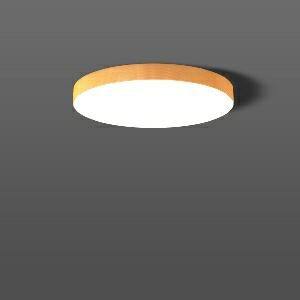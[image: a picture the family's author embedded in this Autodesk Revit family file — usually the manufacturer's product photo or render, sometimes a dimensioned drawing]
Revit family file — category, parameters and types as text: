
# Revit family: flatliner_slim_312281_002_1_76_adea
name_source: partatom
category: Lighting Fixtures
units: mm (PartAtom-declared; Revit-internal decimal feet)

## family parameters
Cut with Voids When Loaded = No
Host = Face
Light Source = No
Part Type = Normal
Room Calculation Point = No
Round Connector Dimension = Use Diameter
Shared = No

## types (1)
- 982556.002 (1 x LED Modul 840, 1700 lm, 4000)
    Apparent Load = 21 VA
    CIE Flux Codes = 45 76 94 95 100
    Color Rendering = 80
    Color Temperature = 4000
    Default Elevation = 1800 mm
    Description = Series: FLATLINER SLIM
Decorative ceiling luminaire for interior decoration. Base luminaire prepared for the installation of fabric lampshade. Base: metal, white, powder-coated. TouchDim sensor capable. Light and/or presence sensors can be integrated. Modular design: with the basic luminaire, a cylindrical fabric lampshade with a polycarbonate satin-finish diffuser must always be ordered separately. Fabric lampshade and diffuser can be assembled without the use of tools. 
Colour: white
Diameter: 317 mm
Height: 34 mm
Lamp: LED exchangeable
Socket: without socket
Colour temperature: 4000K
Colour rendering index (CRI): 80
System power: 19 W
Rated luminous flux: 1700 lm
Beam angle Down: 117°
Luminous efficiency: 89 lm/W
Control gear: AC power, DALI dimmable
Protection class: I
Type of protection: IP 20
    Height = 34 mm  [stored 0.111549 ft]
    Lamp = 1 x LED Modul 840
    Lamp Light Flux = 1700 lm
    Lamp count = 1
    Length = 317 mm
    Lifetime = 50000 h
    Luminous efficacy = 81 lm/W
    Manufacturer = RZB
    ModVariant = No
    Model = 312281.002.1.76
    Mounting Place = Ceiling
    Mounting Type = Surface mounted
    Number of Poles = 1
    OnlyDefault = Yes
    Power Factor = 1
    Product Name = FLATLINER SLIM
    Product group = Surface mounted ceiling Fabric lampshade luminaires
    ProductGroupID = 313
    Protection Class = Protection class I
    Protection Degree = IP 20
    RLX_Detail_Level = 1
    RLX_Emergency_Light_Flux = 0 lm
    RLX_Emergency_Type = 0
    RLX_Emergency_Type_DB = No
    RlxData = <blob elided: 25381 chars, md5=12ecda9a>
    Socket = socket
    Standby Power = 0 W
    System Light Flux = 1700 lm
    System Power = 21 W
    Type Image = 312287.002_982442.0063_982444.002.jpg
    URL = http://relux.com
    VarID = 982556_002_eb81
    Voltage = 230 V
    Voltage Range = 220-240 V
    Weight = 0.00 kg
    Width = 0 mm  [stored 0 ft]

note: [stored X ft] marks values corroborated as IEEE doubles in the binary element streams (Revit-internal decimal feet)

## geometry (parser evidence)
native form markers: Blend x4, Sweep x14
no freeform markers — native parametric forms only
